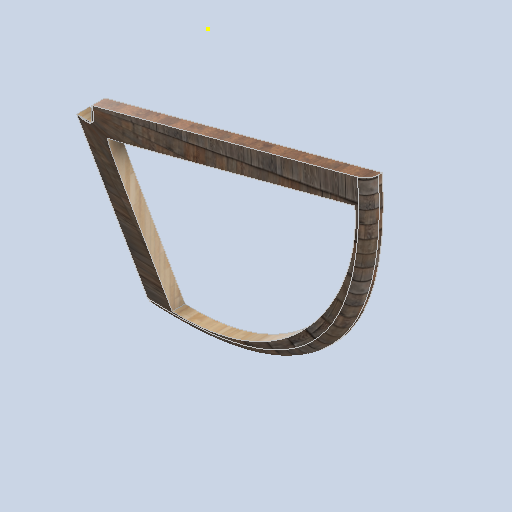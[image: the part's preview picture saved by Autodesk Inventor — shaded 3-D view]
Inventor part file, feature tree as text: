
AUTODESK INVENTOR PART (.ipt)
format: ipt  version: 2024.2 (Build 282272000, 272)  size: 482,816 bytes
history: native  units: mm
features: sketch x13, plane x8, extrude x3, projected_geometry x3, other x2, loft x1, fillet x1
ambient origin geometry x8: Origin, YZ Plane, XZ Plane, XY Plane, X Axis, Y Axis, Z Axis, Center Point
bodies: Solid1 (feature_tree)
feature tree (31):
  sketch  "Sketch1"  dims[d0=175.0mm d1=150.0mm]
  plane  "Work Plane2"
  sketch  "Sketch2"  dims[d2=-2349.0mm d3=12.217305mm]
  plane  "Work Plane3"
  extrude  "Extrusion1"  Depth=150.0mm
  sketch  "Sketch4"  dims[d7=175.0mm d8=150.0mm d9=2349.0mm]
  plane  "Work Plane4"
  sketch  "Sketch5"  dims[d11=12.217305mm]
  plane  "Work Plane5"
  extrude  "Extrusion2"  Depth=12.217305mm
  plane  "Work Plane6"
  sketch  "Sketch7"  dims[d14=0.0mm]
  plane  "Work Plane7"
  plane  "Work Plane8"
  sketch  "Sketch9"  dims[d16=90.0deg]
  sketch  "Sketch8"  dims[d15=2000.0mm]
  sketch  "Sketch10"  dims[d17=150.0mm]
  sketch  "Sketch11"  dims[d18=0.0mm d19=90.0deg]
  loft  "Loft1"
  sketch  "Sketch12"  dims[d20=0.0mm d21=90.0deg]
  extrude  "Extrusion3"  Depth=150.0mm
  fillet  "Fillet1"  Radius=2349.0mm
  sketch  "Sketch14"  dims[d22=0.0mm d23=90.0deg d24=120.0mm d25=120.0mm d26=120.0mm d27=120.0mm d28=120.0mm d29=120.0mm d30=2000.0mm d31=0.0mm d32=0.0mm d33=150.0mm]
  plane  "Work Plane1"
  sketch  "Sketch3"  dims[d4=12.217305mm d5=175.0mm d6=0.0mm]
  sketch  "Sketch6"  dims[d12=175.0mm d13=0.0mm]
  projected_geometry  "Projected Loop1"
  projected_geometry  "Projected Loop2"
  other  "Edges1"
  other  "Edges2"
  projected_geometry  "Projected Loop3"
